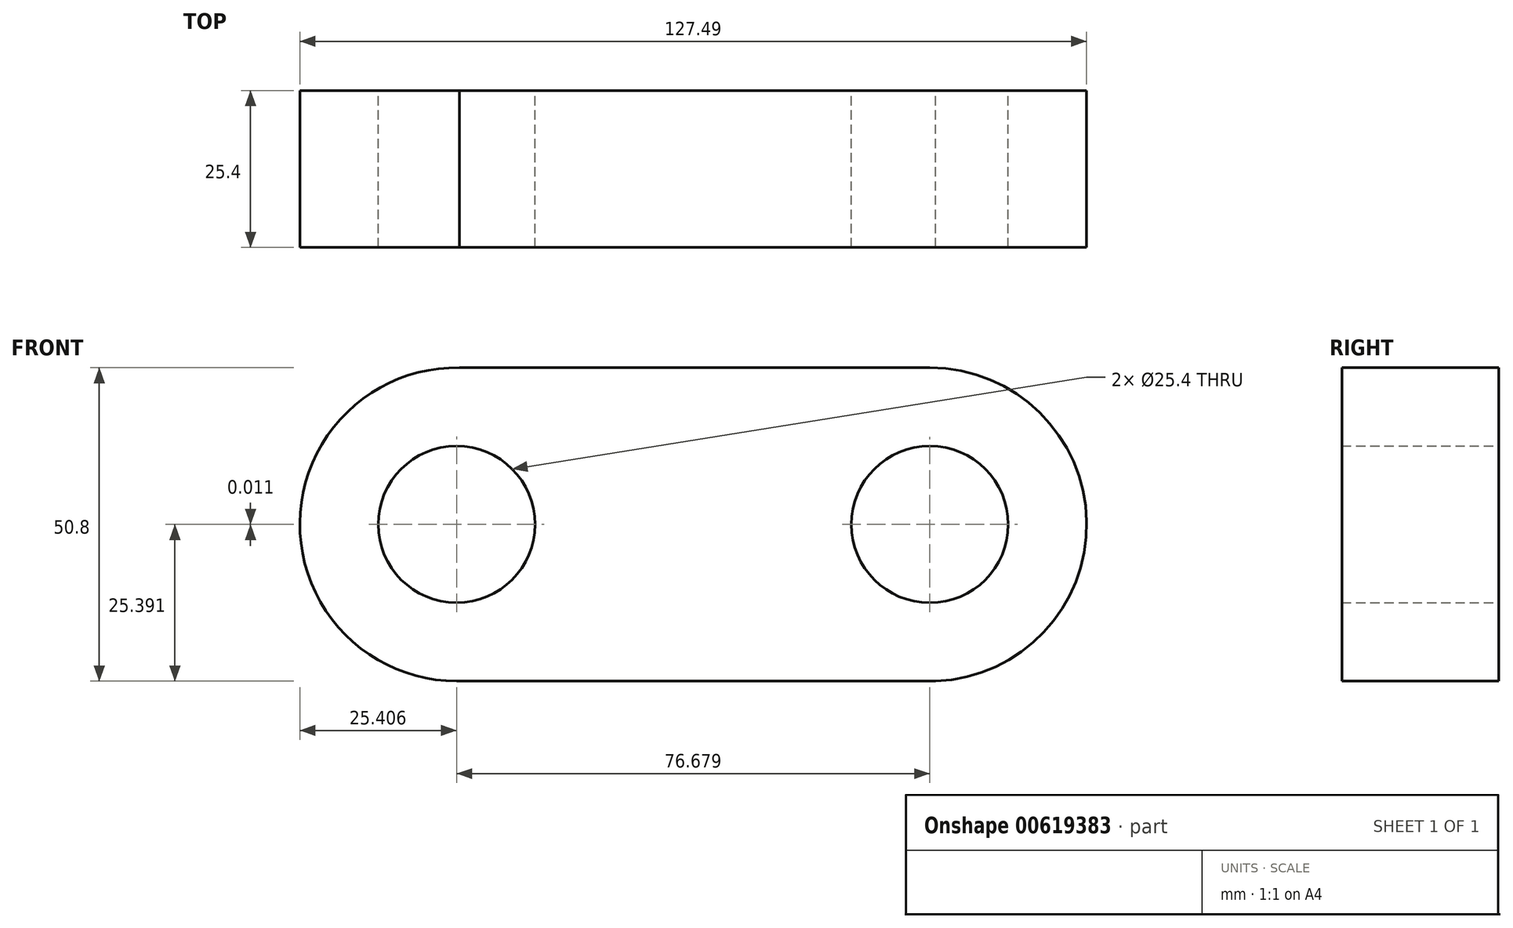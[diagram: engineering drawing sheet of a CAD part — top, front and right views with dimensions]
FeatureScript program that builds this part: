
annotation { "Feature Type Name" : "Feature", "Feature Type Description" : "" }
export const myFeature = defineFeature(function(context is Context, id is Id, definition is map)
    precondition{}
    {
        {
            var Q0;
            Q0=qCreatedBy(makeId("Front.planeOp"),FACE);
            var sketch = newSketch(context, id + "F0", { "sketchPlane" : qUnion([Q0])});
            skLineSegment(sketch, "E0", {"start": v(-25.9, 50.8) * mm, "end": v(50.3, 50.8) * mm});
            skLineSegment(sketch, "E1", {"start": v(-26.38, 0) * mm, "end": v(51.25, 0) * mm});
            skArc(sketch, "E2", {"start": v(-25.9, 50.8) * mm, "mid": v(-51.78, 25.64) * mm, "end": v(-26.38, 0) * mm});
            skArc(sketch, "E3", {"start": v(51.25, 0) * mm, "mid": v(75.7, 25.87) * mm, "end": v(50.3, 50.8) * mm});
            skCircle(sketch, "E4", {"center": v(-26.38, 25.4) * mm, "radius": 12.7 * mm});
            skCircle(sketch, "E5", {"center": v(50.3, 25.4) * mm, "radius": 12.7 * mm});
            skSolve(sketch);
        }
        {
            var Q0;
            Q0=makeQuery(id+"F0.imprint","IMPRINT",FACE,{"disambiguationData":[TD([[makeQuery(id+"F0.imprint","IMPRINT",EDGE,{"derivedFrom":sQuery(id+"F0.wireOp",EDGE,"E0")}),-1.0]])]});
            extrude(context, id + "F1", {"entities" : qUnion([Q0]), "depth" : 25.4 * mm, "offsetDistance" : 25.4 * mm});
        }
    });
